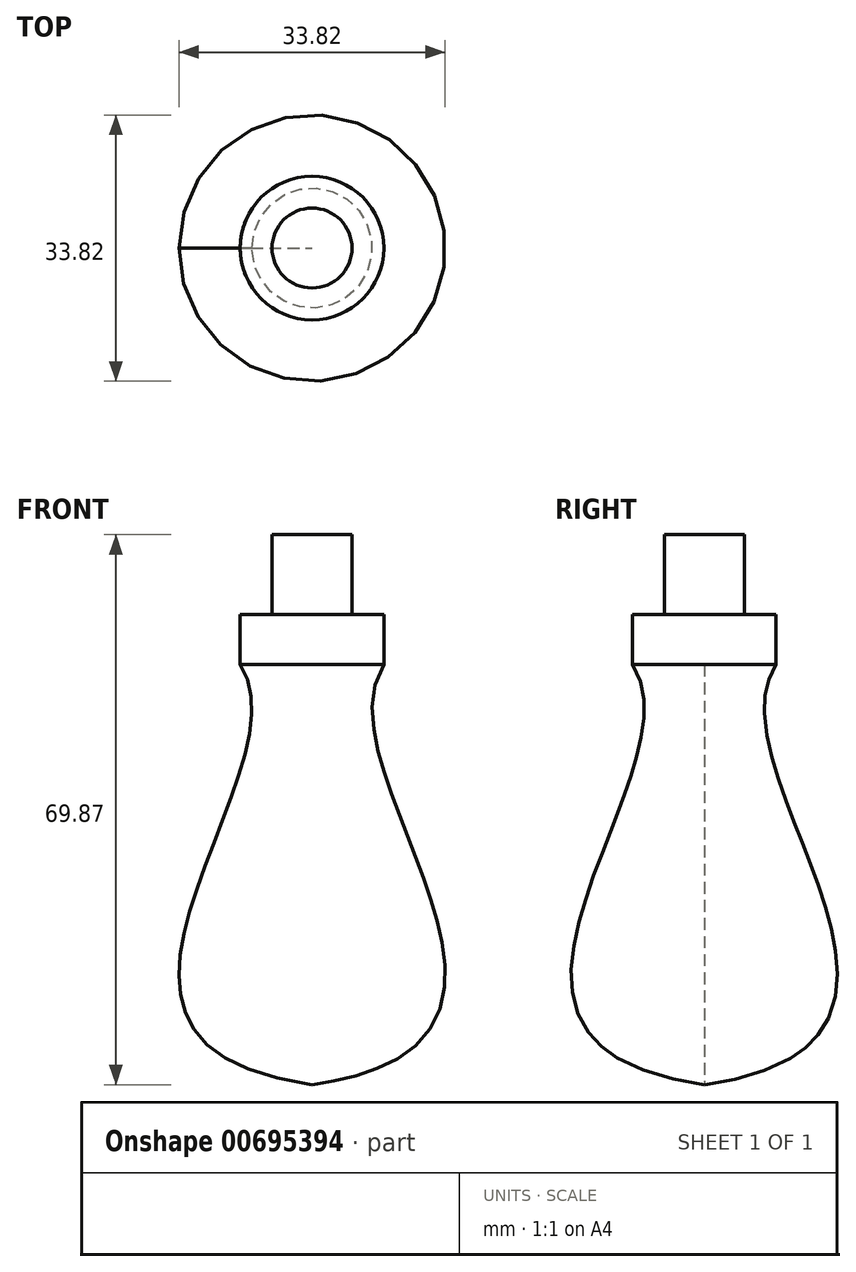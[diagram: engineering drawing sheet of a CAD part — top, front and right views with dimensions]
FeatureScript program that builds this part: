
annotation { "Feature Type Name" : "Feature", "Feature Type Description" : "" }
export const myFeature = defineFeature(function(context is Context, id is Id, definition is map)
    precondition{}
    {
        {
            var Q0;
            Q0=qCreatedBy(makeId("Top.planeOp"),FACE);
            var sketch = newSketch(context, id + "F0", { "sketchPlane" : qUnion([Q0])});
            skCircle(sketch, "E0", {"center": v(0, 0) * mm, "radius": 5.08 * mm});
            skSolve(sketch);
        }
        {
            var Q0;
            Q0=makeQuery(id+"F0.imprint","IMPRINT",FACE,{"disambiguationData":[TD([[makeQuery(id+"F0.imprint","IMPRINT",EDGE,{"derivedFrom":sQuery(id+"F0.wireOp",EDGE,"E0")}),1.0]])]});
            extrude(context, id + "F1", {"entities" : qUnion([Q0]), "depth" : 10.16 * mm, "offsetDistance" : 25.4 * mm});
        }
        {
            var Q0;
            Q0=makeQuery(id+"F1.opExtrude","CAP_FACE",FACE,{"disambiguationData":[OSD([sQuery(id+"F0.wireOp",EDGE,"E0")])],"isStart":true});
            var sketch = newSketch(context, id + "F2", { "sketchPlane" : qUnion([Q0])});
            skCircle(sketch, "E1", {"center": v(0, 0) * mm, "radius": 9.12 * mm});
            skSolve(sketch);
        }
        {
            var Q0;
            Q0=makeQuery(id+"F2.imprint","IMPRINT",FACE,{"disambiguationData":[TD([[makeQuery(id+"F2.imprint","IMPRINT",EDGE,{"derivedFrom":sQuery(id+"F2.wireOp",EDGE,"E1")}),1.0]])]});
            var Q1;
            Q1=makeQuery(id+"F2.imprint","IMPRINT",FACE,{"disambiguationData":[TD([[makeQuery(id+"F2.imprint","IMPRINT",EDGE,{"derivedFrom":makeQuery(id+"F1.opExtrude","CAP_EDGE",EDGE,{"disambiguationData":[OSD([sQuery(id+"F0.wireOp",EDGE,"E0")])],"isStart":true})}),-1.0]])]});
            extrude(context, id + "F3", {"entities" : qUnion([Q0, Q1]), "operationType" : NewBodyOperationType.ADD, "depth" : 6.35 * mm, "offsetDistance" : 25.4 * mm});
        }
        {
            var Q0;
            Q0=qCreatedBy(makeId("Front.planeOp"),FACE);
            var sketch = newSketch(context, id + "F4", { "sketchPlane" : qUnion([Q0])});
            skFitSpline(sketch, "E2", {"points": [v(-9.12, -6.35) * mm, v(0, -59.7) * mm], "startDerivative": vector(27.36, -41.21) * mm, "endDerivative": vector(111.7, -15.43) * mm});
            skLineSegment(sketch, "E3", {"start": v(0, -59.7) * mm, "end": v(0, -6.35) * mm});
            skLineSegment(sketch, "E4", {"start": v(0, -6.35) * mm, "end": v(-9.12, -6.35) * mm});
            skSolve(sketch);
        }
        {
            var Q0;
            Q0=makeQuery(id+"F4.imprint","IMPRINT",FACE,{"disambiguationData":[TD([[makeQuery(id+"F4.imprint","IMPRINT",EDGE,{"derivedFrom":sQuery(id+"F4.wireOp",EDGE,"E2")}),1.0]])]});
            var Q1;
            Q1=sQuery(id+"F4.wireOp",EDGE,"E3");
            revolve(context, id + "F5", {"operationType" : NewBodyOperationType.ADD, "entities" : qUnion([Q0]), "axis" : qUnion([Q1]), "revolveType" : RevolveType.FULL});
        }
    });
